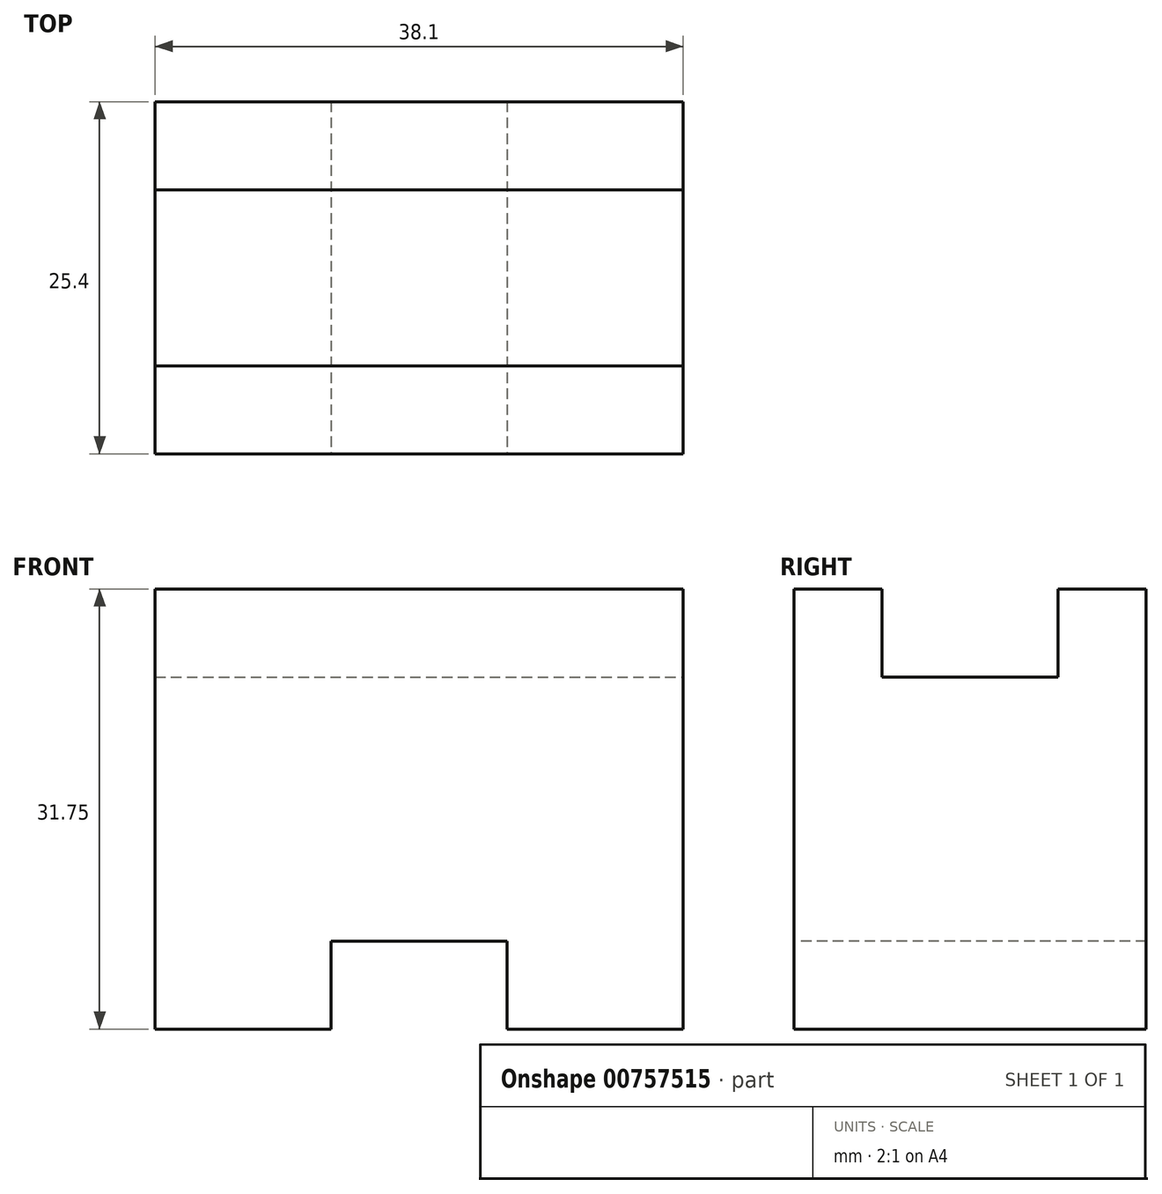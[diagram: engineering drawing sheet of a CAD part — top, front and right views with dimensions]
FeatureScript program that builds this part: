
annotation { "Feature Type Name" : "Feature", "Feature Type Description" : "" }
export const myFeature = defineFeature(function(context is Context, id is Id, definition is map)
    precondition{}
    {
        {
            var Q0;
            Q0=qCreatedBy(makeId("Front.planeOp"),FACE);
            var sketch = newSketch(context, id + "F0", { "sketchPlane" : qUnion([Q0])});
            skLineSegment(sketch, "E0", {"start": v(0, 0) * mm, "end": v(0, 31.75) * mm});
            skLineSegment(sketch, "E1", {"start": v(0, 31.75) * mm, "end": v(-38.1, 31.75) * mm});
            skLineSegment(sketch, "E2", {"start": v(-38.1, 31.75) * mm, "end": v(-38.1, 0) * mm});
            skLineSegment(sketch, "E3", {"start": v(-38.1, 0) * mm, "end": v(0, 0) * mm});
            skSolve(sketch);
        }
        {
            var Q0;
            Q0 = qSketchRegion(id + "F0", true);
            extrude(context, id + "F1", {"entities" : qUnion([Q0]), "depth" : 25.4 * mm, "offsetDistance" : 25.4 * mm});
        }
        {
            var Q0;
            Q0=makeQuery(id+"F1.opExtrude","SWEPT_FACE",FACE,{"disambiguationData":[OSD([sQuery(id+"F0.wireOp",EDGE,"E0")])]});
            var sketch = newSketch(context, id + "F2", { "sketchPlane" : qUnion([Q0])});
            skLineSegment(sketch, "E4", {"start": v(-19.05, 31.75) * mm, "end": v(-19.05, 25.4) * mm});
            skLineSegment(sketch, "E5", {"start": v(-19.05, 25.4) * mm, "end": v(-6.35, 25.4) * mm});
            skLineSegment(sketch, "E6", {"start": v(-6.35, 25.4) * mm, "end": v(-6.35, 31.75) * mm});
            skSolve(sketch);
        }
        {
            var Q0;
            {var subQ0=sQuery(id+"F2.wireOp",EDGE,"E4");Q0=makeQuery(id+"F2.imprint","IMPRINT",FACE,{"disambiguationData":[TD([[makeQuery(id+"F2.imprint","IMPRINT",EDGE,{"derivedFrom":subQ0}),1.0]])]});}
            extrude(context, id + "F3", {"entities" : qUnion([Q0]), "operationType" : NewBodyOperationType.REMOVE, "endBound" : BoundingType.THROUGH_ALL, "oppositeDirection" : true, "depth" : 25.4 * mm, "offsetDistance" : 25.4 * mm});
        }
        {
            var Q0;
            Q0=makeQuery(id+"F1.opExtrude","CAP_FACE",FACE,{"disambiguationData":[OSD([sQuery(id+"F0.wireOp",EDGE,"E0"),sQuery(id+"F0.wireOp",EDGE,"E1"),sQuery(id+"F0.wireOp",EDGE,"E2"),sQuery(id+"F0.wireOp",EDGE,"E3")])],"isStart":false});
            var sketch = newSketch(context, id + "F4", { "sketchPlane" : qUnion([Q0])});
            skLineSegment(sketch, "E7", {"start": v(-25.4, 0) * mm, "end": v(-25.4, 6.35) * mm});
            skLineSegment(sketch, "E8", {"start": v(-25.4, 6.35) * mm, "end": v(-12.7, 6.35) * mm});
            skLineSegment(sketch, "E9", {"start": v(-12.7, 6.35) * mm, "end": v(-12.7, 0) * mm});
            skSolve(sketch);
        }
        {
            var Q0;
            {var subQ0=sQuery(id+"F4.wireOp",EDGE,"E7");Q0=makeQuery(id+"F4.imprint","IMPRINT",FACE,{"disambiguationData":[TD([[makeQuery(id+"F4.imprint","IMPRINT",EDGE,{"derivedFrom":subQ0}),-1.0]])]});}
            extrude(context, id + "F5", {"entities" : qUnion([Q0]), "operationType" : NewBodyOperationType.REMOVE, "endBound" : BoundingType.THROUGH_ALL, "oppositeDirection" : true, "depth" : 25.4 * mm, "offsetDistance" : 25.4 * mm});
        }
    });
